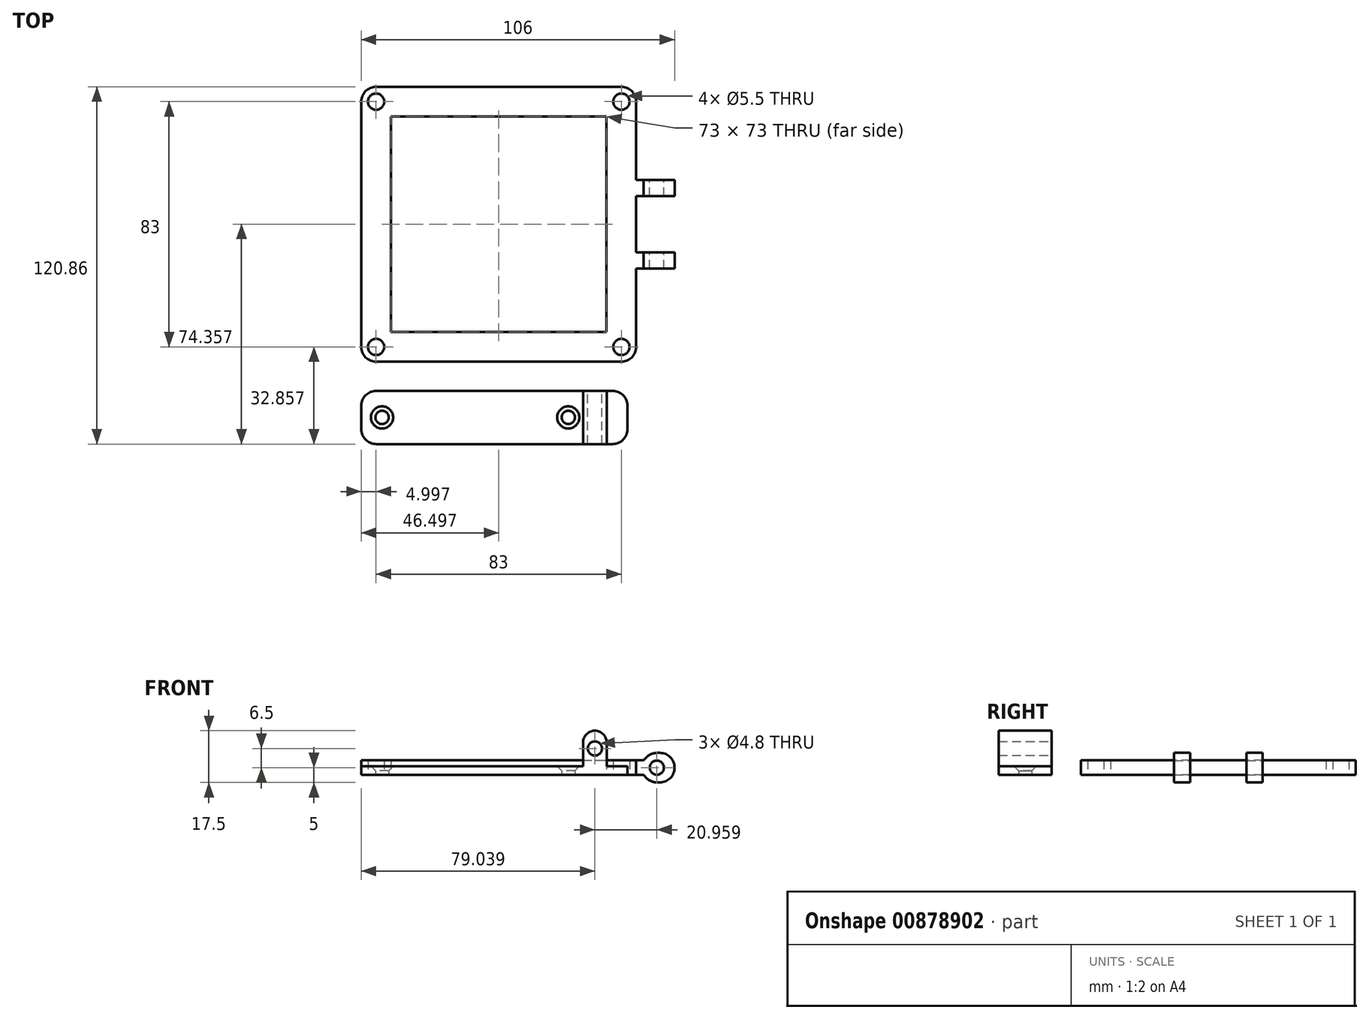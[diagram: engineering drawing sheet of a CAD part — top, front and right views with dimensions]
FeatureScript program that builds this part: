
annotation { "Feature Type Name" : "Feature", "Feature Type Description" : "" }
export const myFeature = defineFeature(function(context is Context, id is Id, definition is map)
    precondition{}
    {
        {
            var Q0;
            Q0=qCreatedBy(makeId("Top.planeOp"),FACE);
            var sketch = newSketch(context, id + "F0", { "sketchPlane" : qUnion([Q0])});
            skCircle(sketch, "E0", {"center": v(-34.68, 0) * mm, "radius": 2.25 * mm});
            skCircle(sketch, "E1", {"center": v(28.32, 0) * mm, "radius": 2.25 * mm});
            skPoint(sketch, "E2.middle", {"position": v(0, 0) * mm});
            skLineSegment(sketch, "E3.bottom", {"start": v(-41.68, 9) * mm, "end": v(48.32, 9) * mm});
            skLineSegment(sketch, "E3.top", {"start": v(-41.68, -9) * mm, "end": v(48.32, -9) * mm});
            skLineSegment(sketch, "E3.left", {"start": v(-41.68, 9) * mm, "end": v(-41.68, -9) * mm});
            skLineSegment(sketch, "E3.right", {"start": v(48.32, 9) * mm, "end": v(48.32, -9) * mm});
            skSolve(sketch);
        }
        {
            var Q0;
            Q0=makeQuery(id+"F0.imprint","IMPRINT",FACE,{"disambiguationData":[TD([[makeQuery(id+"F0.imprint","IMPRINT",EDGE,{"derivedFrom":sQuery(id+"F0.wireOp",EDGE,"E0")}),-1.0]])]});
            extrude(context, id + "F1", {"entities" : qUnion([Q0]), "depth" : 3 * mm, "offsetDistance" : 25 * mm});
        }
        {
            var Q0;
            Q0=makeQuery(id+"F1.opExtrude","CAP_FACE",FACE,{"disambiguationData":[OSD([sQuery(id+"F0.wireOp",EDGE,"E0"),sQuery(id+"F0.wireOp",EDGE,"E1"),sQuery(id+"F0.wireOp",EDGE,"E3.bottom"),sQuery(id+"F0.wireOp",EDGE,"E3.top"),sQuery(id+"F0.wireOp",EDGE,"E3.left"),sQuery(id+"F0.wireOp",EDGE,"E3.right")])],"isStart":false});
            var sketch = newSketch(context, id + "F2", { "sketchPlane" : qUnion([Q0])});
            skLineSegment(sketch, "E4.bottom", {"start": v(33.32, 9) * mm, "end": v(41.32, 9) * mm});
            skLineSegment(sketch, "E4.top", {"start": v(33.32, -9) * mm, "end": v(41.32, -9) * mm});
            skLineSegment(sketch, "E4.left", {"start": v(33.32, 9) * mm, "end": v(33.32, -9) * mm});
            skLineSegment(sketch, "E4.right", {"start": v(41.32, 9) * mm, "end": v(41.32, -9) * mm});
            skCircle(sketch, "E5", {"center": v(-34.68, 0) * mm, "radius": 2.25 * mm});
            skLineSegment(sketch, "E6", {"start": v(-41.68, 9) * mm, "end": v(-41.68, -9) * mm});
            skLineSegment(sketch, "E7", {"start": v(-41.68, 9) * mm, "end": v(48.32, 9) * mm});
            skLineSegment(sketch, "E8", {"start": v(48.32, 9) * mm, "end": v(48.32, -9) * mm});
            skLineSegment(sketch, "E9", {"start": v(-41.68, -9) * mm, "end": v(48.32, -9) * mm});
            skCircle(sketch, "E10", {"center": v(28.32, 0) * mm, "radius": 2.25 * mm});
            skSolve(sketch);
        }
        {
            var Q0;
            {var subQ0=sQuery(id+"F2.wireOp",EDGE,"E4.left");Q0=makeQuery(id+"F2.imprint","IMPRINT",FACE,{"disambiguationData":[TD([[makeQuery(id+"F2.imprint","IMPRINT",EDGE,{"derivedFrom":subQ0}),1.0]])]});}
            extrude(context, id + "F3", {"entities" : qUnion([Q0]), "operationType" : NewBodyOperationType.ADD, "depth" : 12 * mm, "offsetDistance" : 25 * mm});
        }
        {
            var Q0;
            Q0=makeQuery(id+"F3.boolean.opBoolean","MERGE",FACE,{"derivedFrom":[makeQuery(id+"F1.opExtrude","SWEPT_FACE",FACE,{"disambiguationData":[OSD([sQuery(id+"F0.wireOp",EDGE,"E3.bottom")])]}),makeQuery(id+"F3.opExtrude","SWEPT_FACE",FACE,{"disambiguationData":[OSD([sQuery(id+"F2.wireOp",EDGE,"E7")])]})]});
            var sketch = newSketch(context, id + "F4", { "sketchPlane" : qUnion([Q0])});
            skCircle(sketch, "E11", {"center": v(-37.32, 9) * mm, "radius": 2.4 * mm});
            skSolve(sketch);
        }
        {
            var Q0;
            Q0=makeQuery(id+"F4.imprint","IMPRINT",FACE,{"disambiguationData":[TD([[makeQuery(id+"F4.imprint","IMPRINT",EDGE,{"derivedFrom":sQuery(id+"F4.wireOp",EDGE,"E11")}),1.0]])]});
            extrude(context, id + "F5", {"entities" : qUnion([Q0]), "operationType" : NewBodyOperationType.REMOVE, "endBound" : BoundingType.UP_TO_NEXT, "oppositeDirection" : true, "depth" : 25 * mm, "offsetDistance" : 25 * mm});
        }
        {
            var Q0;
            Q0=makeQuery(id+"F1.opExtrude","CAP_EDGE",EDGE,{"disambiguationData":[OSD([sQuery(id+"F0.wireOp",EDGE,"E0")])],"isStart":false});
            var Q1;
            Q1=makeQuery(id+"F1.opExtrude","CAP_EDGE",EDGE,{"disambiguationData":[OSD([sQuery(id+"F0.wireOp",EDGE,"E1")])],"isStart":false});
            chamfer(context, id + "F6", {"entities" : qUnion([Q0, Q1]), "width" : 1.5 * mm, "tangentPropagation" : true});
        }
        {
            var Q0;
            Q0=qCreatedBy(makeId("Top.planeOp"),FACE);
            var sketch = newSketch(context, id + "F7", { "sketchPlane" : qUnion([Q0])});
            skLineSegment(sketch, "E12.bottom", {"start": v(-36.72, 106.86) * mm, "end": v(46.28, 106.86) * mm, "construction": true});
            skLineSegment(sketch, "E12.top", {"start": v(-36.72, 23.86) * mm, "end": v(46.28, 23.86) * mm, "construction": true});
            skLineSegment(sketch, "E12.left", {"start": v(-36.72, 106.86) * mm, "end": v(-36.72, 23.86) * mm, "construction": true});
            skLineSegment(sketch, "E12.right", {"start": v(46.28, 106.86) * mm, "end": v(46.28, 23.86) * mm, "construction": true});
            skLineSegment(sketch, "E13.bottom", {"start": v(-41.72, 111.86) * mm, "end": v(51.28, 111.86) * mm});
            skLineSegment(sketch, "E13.top", {"start": v(-41.72, 18.86) * mm, "end": v(51.28, 18.86) * mm});
            skLineSegment(sketch, "E13.left", {"start": v(-41.72, 111.86) * mm, "end": v(-41.72, 18.86) * mm});
            skLineSegment(sketch, "E13.right", {"start": v(51.28, 111.86) * mm, "end": v(51.28, 18.86) * mm});
            skCircle(sketch, "E14", {"center": v(46.28, 106.86) * mm, "radius": 2.75 * mm});
            skCircle(sketch, "E15", {"center": v(-36.72, 106.86) * mm, "radius": 2.75 * mm});
            skCircle(sketch, "E16", {"center": v(-36.72, 23.86) * mm, "radius": 2.75 * mm});
            skCircle(sketch, "E17", {"center": v(46.28, 23.86) * mm, "radius": 2.75 * mm});
            skLineSegment(sketch, "E18.bottom", {"start": v(-31.72, 101.86) * mm, "end": v(41.28, 101.86) * mm});
            skLineSegment(sketch, "E18.top", {"start": v(-31.72, 28.86) * mm, "end": v(41.28, 28.86) * mm});
            skLineSegment(sketch, "E18.left", {"start": v(-31.72, 101.86) * mm, "end": v(-31.72, 28.86) * mm});
            skLineSegment(sketch, "E18.right", {"start": v(41.28, 101.86) * mm, "end": v(41.28, 28.86) * mm});
            skSolve(sketch);
        }
        {
            var Q0;
            Q0=makeQuery(id+"F7.imprint","IMPRINT",FACE,{"disambiguationData":[TD([[makeQuery(id+"F7.imprint","IMPRINT",EDGE,{"derivedFrom":sQuery(id+"F7.wireOp",EDGE,"E13.bottom")}),-1.0]])]});
            extrude(context, id + "F8", {"entities" : qUnion([Q0]), "depth" : 5 * mm, "offsetDistance" : 25 * mm});
        }
        {
            var Q0;
            Q0=makeQuery(id+"F8.opExtrude","SWEPT_FACE",FACE,{"disambiguationData":[OSD([sQuery(id+"F7.wireOp",EDGE,"E13.right")])]});
            var sketch = newSketch(context, id + "F9", { "sketchPlane" : qUnion([Q0])});
            skLineSegment(sketch, "E19.bottom", {"start": v(80.36, -2.5) * mm, "end": v(50.36, -2.5) * mm});
            skLineSegment(sketch, "E19.top", {"start": v(80.36, 7.5) * mm, "end": v(50.36, 7.5) * mm});
            skLineSegment(sketch, "E19.left", {"start": v(80.36, -2.5) * mm, "end": v(80.36, 7.5) * mm});
            skLineSegment(sketch, "E19.right", {"start": v(50.36, -2.5) * mm, "end": v(50.36, 7.5) * mm});
            skPoint(sketch, "E19.middle", {"position": v(65.36, 2.5) * mm});
            skPoint(sketch, "E19.middle.positionSnap0", {"position": v(111.86, 2.5) * mm});
            skPoint(sketch, "E19.centerSnap0", {"position": v(111.86, 2.5) * mm});
            skLineSegment(sketch, "E20.bottom", {"start": v(74.86, -2.5) * mm, "end": v(55.86, -2.5) * mm});
            skLineSegment(sketch, "E20.top", {"start": v(74.86, 7.5) * mm, "end": v(55.86, 7.5) * mm});
            skLineSegment(sketch, "E20.left", {"start": v(74.86, -2.5) * mm, "end": v(74.86, 7.5) * mm});
            skLineSegment(sketch, "E20.right", {"start": v(55.86, -2.5) * mm, "end": v(55.86, 7.5) * mm});
            skSolve(sketch);
        }
        {
            var Q0;
            {var subQ0=sQuery(id+"F9.wireOp",EDGE,"E19.right");var subQ1=sQuery(id+"F7.wireOp",EDGE,"E13.right");var subQ2=makeQuery(id+"F8.opExtrude","CAP_EDGE",EDGE,{"disambiguationData":[OSD([subQ1])],"isStart":true});var subQ3=makeQuery(id+"F9.imprint","INTERSECT",VERTEX,{"derivedFrom":[subQ2,subQ0]});Q0=makeQuery(id+"F9.imprint","IMPRINT",FACE,{"disambiguationData":[TD([[makeQuery(id+"F9.imprint","IMPRINT",EDGE,{"disambiguationData":[TD([[subQ3,-1.0]])],"derivedFrom":subQ0}),-1.0]])]});}
            var Q1;
            {var subQ0=sQuery(id+"F9.wireOp",EDGE,"E19.right");var subQ1=sQuery(id+"F9.wireOp",EDGE,"E19.bottom");var subQ2=makeQuery(id+"F9.imprint","INTERSECT",VERTEX,{"derivedFrom":[subQ1,subQ0]});Q1=makeQuery(id+"F9.imprint","IMPRINT",FACE,{"disambiguationData":[TD([[makeQuery(id+"F9.imprint","IMPRINT",EDGE,{"disambiguationData":[TD([[subQ2,-1.0]])],"derivedFrom":subQ0}),-1.0]])]});}
            var Q2;
            {var subQ0=sQuery(id+"F9.wireOp",EDGE,"E19.left");var subQ1=sQuery(id+"F9.wireOp",EDGE,"E19.top");var subQ2=makeQuery(id+"F9.imprint","INTERSECT",VERTEX,{"derivedFrom":[subQ1,subQ0]});Q2=makeQuery(id+"F9.imprint","IMPRINT",FACE,{"disambiguationData":[TD([[makeQuery(id+"F9.imprint","IMPRINT",EDGE,{"disambiguationData":[TD([[subQ2,1.0]])],"derivedFrom":subQ0}),1.0]])]});}
            var Q3;
            {var subQ0=sQuery(id+"F9.wireOp",EDGE,"E19.left");var subQ1=sQuery(id+"F9.wireOp",EDGE,"E19.bottom");var subQ2=makeQuery(id+"F9.imprint","INTERSECT",VERTEX,{"derivedFrom":[subQ1,subQ0]});Q3=makeQuery(id+"F9.imprint","IMPRINT",FACE,{"disambiguationData":[TD([[makeQuery(id+"F9.imprint","IMPRINT",EDGE,{"disambiguationData":[TD([[subQ2,-1.0]])],"derivedFrom":subQ0}),1.0]])]});}
            var Q4;
            {var subQ0=sQuery(id+"F9.wireOp",EDGE,"E19.left");var subQ1=sQuery(id+"F7.wireOp",EDGE,"E13.right");var subQ2=makeQuery(id+"F8.opExtrude","CAP_EDGE",EDGE,{"disambiguationData":[OSD([subQ1])],"isStart":true});var subQ3=makeQuery(id+"F9.imprint","INTERSECT",VERTEX,{"derivedFrom":[subQ2,subQ0]});Q4=makeQuery(id+"F9.imprint","IMPRINT",FACE,{"disambiguationData":[TD([[makeQuery(id+"F9.imprint","IMPRINT",EDGE,{"disambiguationData":[TD([[subQ3,-1.0]])],"derivedFrom":subQ0}),1.0]])]});}
            var Q5;
            {var subQ0=sQuery(id+"F9.wireOp",EDGE,"E19.right");var subQ1=sQuery(id+"F9.wireOp",EDGE,"E19.top");var subQ2=makeQuery(id+"F9.imprint","INTERSECT",VERTEX,{"derivedFrom":[subQ1,subQ0]});Q5=makeQuery(id+"F9.imprint","IMPRINT",FACE,{"disambiguationData":[TD([[makeQuery(id+"F9.imprint","IMPRINT",EDGE,{"disambiguationData":[TD([[subQ2,1.0]])],"derivedFrom":subQ0}),-1.0]])]});}
            extrude(context, id + "F10", {"entities" : qUnion([Q0, Q1, Q2, Q3, Q4, Q5]), "operationType" : NewBodyOperationType.ADD, "depth" : 13 * mm, "offsetDistance" : 25 * mm});
        }
        {
            var Q0;
            Q0=makeQuery(id+"F10.opExtrude","SWEPT_FACE",FACE,{"disambiguationData":[OSD([sQuery(id+"F9.wireOp",EDGE,"E19.left")])]});
            var sketch = newSketch(context, id + "F11", { "sketchPlane" : qUnion([Q0])});
            skCircle(sketch, "E21", {"center": v(-58.28, 2.5) * mm, "radius": 2.4 * mm});
            skPoint(sketch, "E21.centerSnap0", {"position": v(-64.28, 2.5) * mm});
            skSolve(sketch);
        }
        {
            var Q0;
            Q0=makeQuery(id+"F11.imprint","IMPRINT",FACE,{"disambiguationData":[TD([[makeQuery(id+"F11.imprint","IMPRINT",EDGE,{"derivedFrom":sQuery(id+"F11.wireOp",EDGE,"E21")}),1.0]])]});
            extrude(context, id + "F12", {"entities" : qUnion([Q0]), "operationType" : NewBodyOperationType.REMOVE, "endBound" : BoundingType.THROUGH_ALL, "oppositeDirection" : true, "depth" : 25 * mm, "offsetDistance" : 25 * mm});
        }
        {
            var Q0;
            {var subQ0=sQuery(id+"F9.wireOp",EDGE,"E19.top");Q0=makeQuery(id+"F10.opExtrude","CAP_EDGE",EDGE,{"disambiguationData":[OSD([subQ0]),TDD([makeQuery(id+"F9.imprint","IMPRINT",EDGE,{"disambiguationData":[TD([[makeQuery(id+"F9.imprint","INTERSECT",VERTEX,{"derivedFrom":[subQ0,sQuery(id+"F9.wireOp",EDGE,"E19.right")]}),1.0]])],"derivedFrom":subQ0})])],"isStart":true});}
            var Q1;
            {var subQ0=sQuery(id+"F9.wireOp",EDGE,"E19.top");Q1=makeQuery(id+"F10.opExtrude","CAP_EDGE",EDGE,{"disambiguationData":[OSD([subQ0]),TDD([makeQuery(id+"F9.imprint","IMPRINT",EDGE,{"disambiguationData":[TD([[makeQuery(id+"F9.imprint","INTERSECT",VERTEX,{"derivedFrom":[subQ0,sQuery(id+"F9.wireOp",EDGE,"E19.left")]}),-1.0]])],"derivedFrom":subQ0})])],"isStart":true});}
            var Q2;
            {var subQ0=sQuery(id+"F9.wireOp",EDGE,"E19.bottom");Q2=makeQuery(id+"F10.opExtrude","CAP_EDGE",EDGE,{"disambiguationData":[OSD([subQ0]),TDD([makeQuery(id+"F9.imprint","IMPRINT",EDGE,{"disambiguationData":[TD([[makeQuery(id+"F9.imprint","INTERSECT",VERTEX,{"derivedFrom":[subQ0,sQuery(id+"F9.wireOp",EDGE,"E19.right")]}),1.0]])],"derivedFrom":subQ0})])],"isStart":true});}
            var Q3;
            {var subQ0=sQuery(id+"F9.wireOp",EDGE,"E19.bottom");Q3=makeQuery(id+"F10.opExtrude","CAP_EDGE",EDGE,{"disambiguationData":[OSD([subQ0]),TDD([makeQuery(id+"F9.imprint","IMPRINT",EDGE,{"disambiguationData":[TD([[makeQuery(id+"F9.imprint","INTERSECT",VERTEX,{"derivedFrom":[subQ0,sQuery(id+"F9.wireOp",EDGE,"E19.left")]}),-1.0]])],"derivedFrom":subQ0})])],"isStart":true});}
            chamfer(context, id + "F13", {"entities" : qUnion([Q0, Q1, Q2, Q3]), "width" : 5 * mm, "tangentPropagation" : true});
        }
        {
            var Q0;
            {var subQ0=sQuery(id+"F9.wireOp",EDGE,"E19.top");Q0=makeQuery(id+"F10.opExtrude","CAP_EDGE",EDGE,{"disambiguationData":[OSD([subQ0]),TDD([makeQuery(id+"F9.imprint","IMPRINT",EDGE,{"disambiguationData":[TD([[makeQuery(id+"F9.imprint","INTERSECT",VERTEX,{"derivedFrom":[subQ0,sQuery(id+"F9.wireOp",EDGE,"E19.right")]}),1.0]])],"derivedFrom":subQ0})])],"isStart":false});}
            var Q1;
            {var subQ0=sQuery(id+"F9.wireOp",EDGE,"E19.top");Q1=makeQuery(id+"F10.opExtrude","CAP_EDGE",EDGE,{"disambiguationData":[OSD([subQ0]),TDD([makeQuery(id+"F9.imprint","IMPRINT",EDGE,{"disambiguationData":[TD([[makeQuery(id+"F9.imprint","INTERSECT",VERTEX,{"derivedFrom":[subQ0,sQuery(id+"F9.wireOp",EDGE,"E19.left")]}),-1.0]])],"derivedFrom":subQ0})])],"isStart":false});}
            var Q2;
            {var subQ0=sQuery(id+"F9.wireOp",EDGE,"E19.bottom");Q2=makeQuery(id+"F10.opExtrude","CAP_EDGE",EDGE,{"disambiguationData":[OSD([subQ0]),TDD([makeQuery(id+"F9.imprint","IMPRINT",EDGE,{"disambiguationData":[TD([[makeQuery(id+"F9.imprint","INTERSECT",VERTEX,{"derivedFrom":[subQ0,sQuery(id+"F9.wireOp",EDGE,"E19.left")]}),-1.0]])],"derivedFrom":subQ0})])],"isStart":false});}
            var Q3;
            {var subQ0=sQuery(id+"F9.wireOp",EDGE,"E19.bottom");Q3=makeQuery(id+"F10.opExtrude","CAP_EDGE",EDGE,{"disambiguationData":[OSD([subQ0]),TDD([makeQuery(id+"F9.imprint","IMPRINT",EDGE,{"disambiguationData":[TD([[makeQuery(id+"F9.imprint","INTERSECT",VERTEX,{"derivedFrom":[subQ0,sQuery(id+"F9.wireOp",EDGE,"E19.right")]}),1.0]])],"derivedFrom":subQ0})])],"isStart":false});}
            var Q4;
            {var subQ0=sQuery(id+"F9.wireOp",EDGE,"E19.top");var subQ1=makeQuery(id+"F9.imprint","IMPRINT",EDGE,{"disambiguationData":[TD([[makeQuery(id+"F9.imprint","INTERSECT",VERTEX,{"derivedFrom":[subQ0,sQuery(id+"F9.wireOp",EDGE,"E19.right")]}),1.0]])],"derivedFrom":subQ0});Q4=makeQuery(id+"F13.opChamfer","BLEND_EDGE",EDGE,{"blendedFrom":[makeQuery(id+"F10.opExtrude","CAP_EDGE",EDGE,{"disambiguationData":[OSD([subQ0]),TDD([subQ1])],"isStart":true}),makeQuery(id+"F10.opExtrude","SWEPT_FACE",FACE,{"disambiguationData":[OSD([subQ0]),TDD([subQ1])]})],"blendedInto":[makeQuery(id+"F10.opExtrude","SWEPT_FACE",FACE,{"disambiguationData":[OSD([subQ0]),TDD([subQ1])]})]});}
            var Q5;
            {var subQ0=sQuery(id+"F9.wireOp",EDGE,"E19.bottom");var subQ1=makeQuery(id+"F9.imprint","IMPRINT",EDGE,{"disambiguationData":[TD([[makeQuery(id+"F9.imprint","INTERSECT",VERTEX,{"derivedFrom":[subQ0,sQuery(id+"F9.wireOp",EDGE,"E19.right")]}),1.0]])],"derivedFrom":subQ0});Q5=makeQuery(id+"F13.opChamfer","BLEND_EDGE",EDGE,{"blendedFrom":[makeQuery(id+"F10.opExtrude","CAP_EDGE",EDGE,{"disambiguationData":[OSD([subQ0]),TDD([subQ1])],"isStart":true}),makeQuery(id+"F10.opExtrude","SWEPT_FACE",FACE,{"disambiguationData":[OSD([subQ0]),TDD([subQ1])]})],"blendedInto":[makeQuery(id+"F10.opExtrude","SWEPT_FACE",FACE,{"disambiguationData":[OSD([subQ0]),TDD([subQ1])]})]});}
            var Q6;
            {var subQ0=sQuery(id+"F9.wireOp",EDGE,"E19.bottom");var subQ1=makeQuery(id+"F9.imprint","IMPRINT",EDGE,{"disambiguationData":[TD([[makeQuery(id+"F9.imprint","INTERSECT",VERTEX,{"derivedFrom":[subQ0,sQuery(id+"F9.wireOp",EDGE,"E19.left")]}),-1.0]])],"derivedFrom":subQ0});Q6=makeQuery(id+"F13.opChamfer","BLEND_EDGE",EDGE,{"blendedFrom":[makeQuery(id+"F10.opExtrude","CAP_EDGE",EDGE,{"disambiguationData":[OSD([subQ0]),TDD([subQ1])],"isStart":true}),makeQuery(id+"F10.opExtrude","SWEPT_FACE",FACE,{"disambiguationData":[OSD([subQ0]),TDD([subQ1])]})],"blendedInto":[makeQuery(id+"F10.opExtrude","SWEPT_FACE",FACE,{"disambiguationData":[OSD([subQ0]),TDD([subQ1])]})]});}
            var Q7;
            {var subQ0=sQuery(id+"F9.wireOp",EDGE,"E19.top");var subQ1=makeQuery(id+"F9.imprint","IMPRINT",EDGE,{"disambiguationData":[TD([[makeQuery(id+"F9.imprint","INTERSECT",VERTEX,{"derivedFrom":[subQ0,sQuery(id+"F9.wireOp",EDGE,"E19.left")]}),-1.0]])],"derivedFrom":subQ0});Q7=makeQuery(id+"F13.opChamfer","BLEND_EDGE",EDGE,{"blendedFrom":[makeQuery(id+"F10.opExtrude","CAP_EDGE",EDGE,{"disambiguationData":[OSD([subQ0]),TDD([subQ1])],"isStart":true}),makeQuery(id+"F10.opExtrude","SWEPT_FACE",FACE,{"disambiguationData":[OSD([subQ0]),TDD([subQ1])]})],"blendedInto":[makeQuery(id+"F10.opExtrude","SWEPT_FACE",FACE,{"disambiguationData":[OSD([subQ0]),TDD([subQ1])]})]});}
            fillet(context, id + "F14", {"entities" : qUnion([Q0, Q1, Q2, Q3, Q4, Q5, Q6, Q7]), "radius" : 5 * mm, "tangentPropagation" : true, "allowEdgeOverflow" : false});
        }
        {
            var Q0;
            Q0=makeQuery(id+"F8.opExtrude","SWEPT_EDGE",EDGE,{"disambiguationData":[OSD([sQuery(id+"F7.wireOp",EDGE,"E13.top"),sQuery(id+"F7.wireOp",EDGE,"E13.right")])]});
            var Q1;
            Q1=makeQuery(id+"F8.opExtrude","SWEPT_EDGE",EDGE,{"disambiguationData":[OSD([sQuery(id+"F7.wireOp",EDGE,"E13.bottom"),sQuery(id+"F7.wireOp",EDGE,"E13.right")])]});
            var Q2;
            Q2=makeQuery(id+"F8.opExtrude","SWEPT_EDGE",EDGE,{"disambiguationData":[OSD([sQuery(id+"F7.wireOp",EDGE,"E13.bottom"),sQuery(id+"F7.wireOp",EDGE,"E13.left")])]});
            var Q3;
            Q3=makeQuery(id+"F8.opExtrude","SWEPT_EDGE",EDGE,{"disambiguationData":[OSD([sQuery(id+"F7.wireOp",EDGE,"E13.top"),sQuery(id+"F7.wireOp",EDGE,"E13.left")])]});
            fillet(context, id + "F15", {"entities" : qUnion([Q0, Q1, Q2, Q3]), "radius" : 5 * mm, "tangentPropagation" : true, "allowEdgeOverflow" : false});
        }
        {
            var Q0;
            Q0=makeQuery(id+"F3.opExtrude","CAP_EDGE",EDGE,{"disambiguationData":[OSD([sQuery(id+"F2.wireOp",EDGE,"E4.right")])],"isStart":false});
            var Q1;
            Q1=makeQuery(id+"F3.opExtrude","CAP_EDGE",EDGE,{"disambiguationData":[OSD([sQuery(id+"F2.wireOp",EDGE,"E4.left")])],"isStart":false});
            fillet(context, id + "F16", {"entities" : qUnion([Q0, Q1]), "radius" : 4 * mm, "tangentPropagation" : true, "allowEdgeOverflow" : false});
        }
        {
            var Q0;
            Q0=makeQuery(id+"F1.opExtrude","SWEPT_EDGE",EDGE,{"disambiguationData":[OSD([sQuery(id+"F0.wireOp",EDGE,"E3.top"),sQuery(id+"F0.wireOp",EDGE,"E3.left")])]});
            var Q1;
            Q1=makeQuery(id+"F1.opExtrude","SWEPT_EDGE",EDGE,{"disambiguationData":[OSD([sQuery(id+"F0.wireOp",EDGE,"E3.bottom"),sQuery(id+"F0.wireOp",EDGE,"E3.left")])]});
            var Q2;
            Q2=makeQuery(id+"F1.opExtrude","SWEPT_EDGE",EDGE,{"disambiguationData":[OSD([sQuery(id+"F0.wireOp",EDGE,"E3.top"),sQuery(id+"F0.wireOp",EDGE,"E3.right")])]});
            var Q3;
            Q3=makeQuery(id+"F1.opExtrude","SWEPT_EDGE",EDGE,{"disambiguationData":[OSD([sQuery(id+"F0.wireOp",EDGE,"E3.bottom"),sQuery(id+"F0.wireOp",EDGE,"E3.right")])]});
            fillet(context, id + "F17", {"entities" : qUnion([Q0, Q1, Q2, Q3]), "radius" : 5 * mm, "tangentPropagation" : true, "allowEdgeOverflow" : false});
        }
    });
